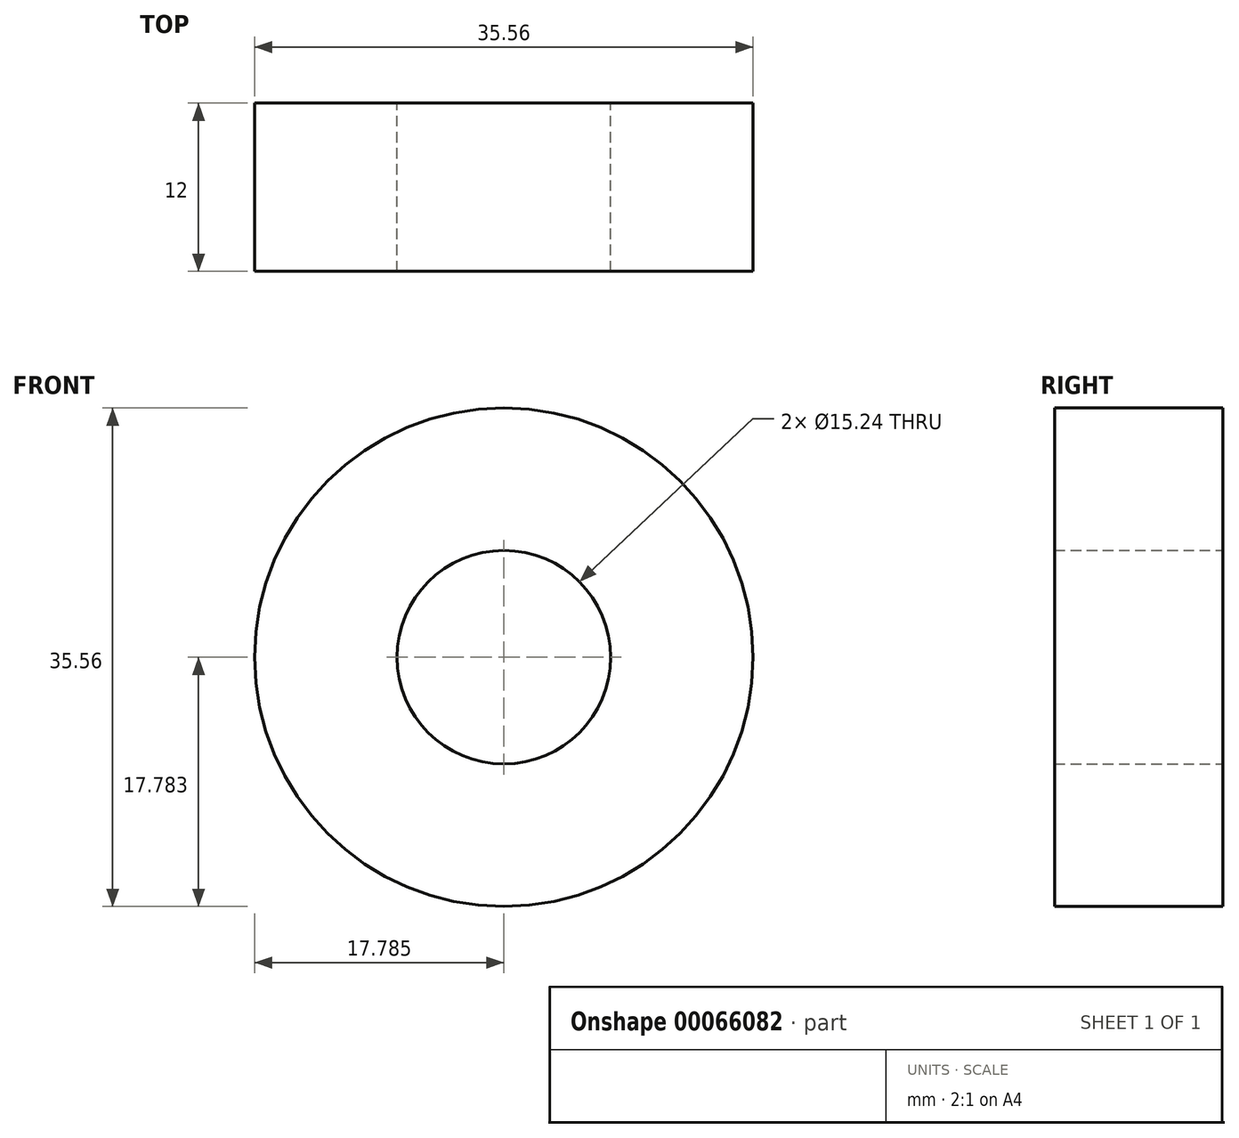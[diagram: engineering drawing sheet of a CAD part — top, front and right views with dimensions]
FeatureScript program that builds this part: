
annotation { "Feature Type Name" : "Feature", "Feature Type Description" : "" }
export const myFeature = defineFeature(function(context is Context, id is Id, definition is map)
    precondition{}
    {
        {
            var Q0;
            Q0=qCreatedBy(makeId("Front.planeOp"),FACE);
            var sketch = newSketch(context, id + "F0", { "sketchPlane" : qUnion([Q0])});
            skPoint(sketch, "E0.rect.middle", {"position": v(-0.72, 20.65) * mm});
            skCircle(sketch, "E1", {"center": v(-0.72, -0.94) * mm, "radius": 17.78 * mm});
            skCircle(sketch, "E2", {"center": v(-0.72, -0.94) * mm, "radius": 7.62 * mm});
            skSolve(sketch);
        }
        {
            var Q0;
            Q0=makeQuery(id+"F0.imprint","IMPRINT",FACE,{"disambiguationData":[TD([[makeQuery(id+"F0.imprint","IMPRINT",EDGE,{"derivedFrom":sQuery(id+"F0.wireOp",EDGE,"E1")}),1.0]])]});
            extrude(context, id + "F1", {"entities" : qUnion([Q0]), "depth" : 12 * mm});
        }
    });
